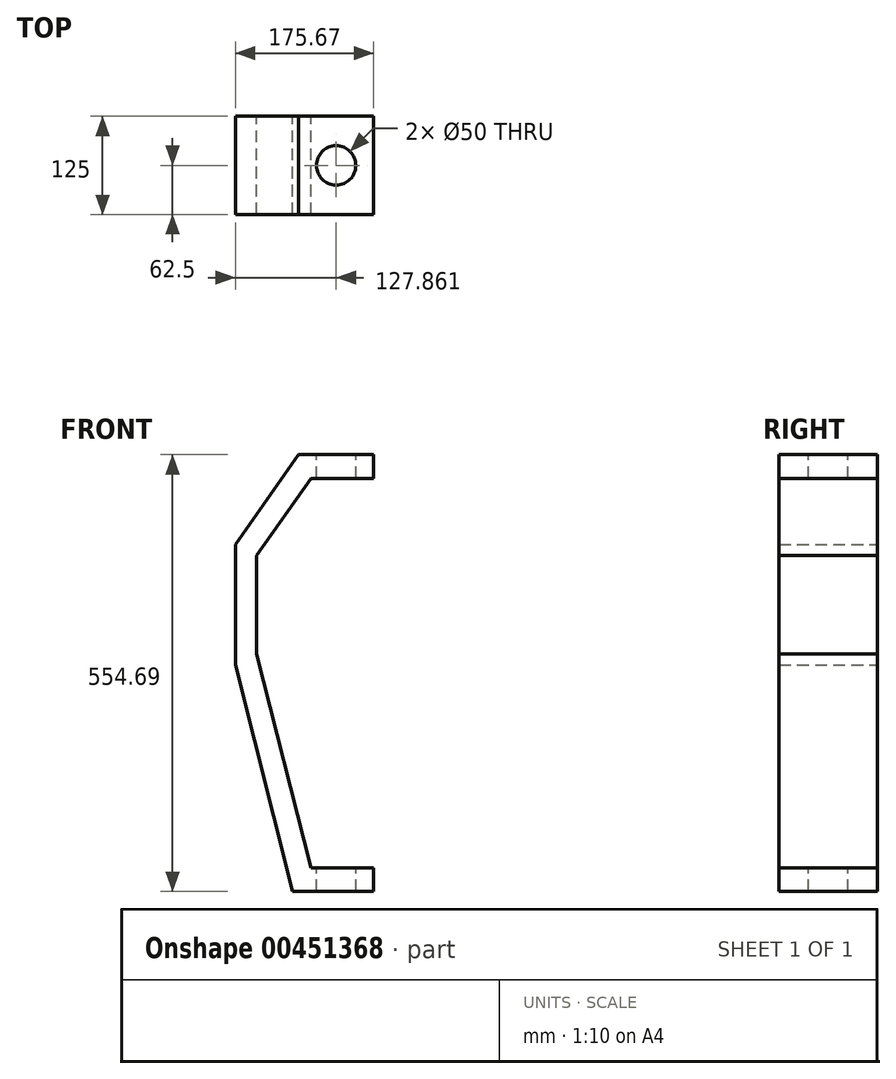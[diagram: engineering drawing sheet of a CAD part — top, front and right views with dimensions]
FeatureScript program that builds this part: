
annotation { "Feature Type Name" : "Feature", "Feature Type Description" : "" }
export const myFeature = defineFeature(function(context is Context, id is Id, definition is map)
    precondition{}
    {
        {
            var Q0;
            Q0=qCreatedBy(makeId("Front.planeOp"),FACE);
            var sketch = newSketch(context, id + "F0", { "sketchPlane" : qUnion([Q0])});
            skLineSegment(sketch, "E0", {"start": v(0, -62.5) * mm, "end": v(0, 62.5) * mm});
            skLineSegment(sketch, "E1", {"start": v(0, 62.5) * mm, "end": v(68.83, 160.8) * mm});
            skLineSegment(sketch, "E2", {"start": v(68.83, 160.8) * mm, "end": v(148.83, 160.8) * mm});
            skLineSegment(sketch, "E3", {"start": v(148.83, 160.8) * mm, "end": v(148.83, 190.8) * mm});
            skLineSegment(sketch, "E4", {"start": v(68.83, 160.8) * mm, "end": v(53.21, 190.8) * mm, "construction": true});
            skLineSegment(sketch, "E5", {"start": v(148.83, 190.8) * mm, "end": v(53.21, 190.8) * mm});
            skLineSegment(sketch, "E6", {"start": v(0, 62.5) * mm, "end": v(-26.84, 76.47) * mm, "construction": true});
            skLineSegment(sketch, "E7", {"start": v(53.21, 190.8) * mm, "end": v(-26.84, 76.47) * mm});
            skLineSegment(sketch, "E8.MirrorCS", {"start": v(0, -62.5) * mm, "end": v(-26.84, -76.47) * mm, "construction": true});
            skLineSegment(sketch, "E9", {"start": v(-26.84, 76.47) * mm, "end": v(-26.84, -76.47) * mm});
            skLineSegment(sketch, "E10", {"start": v(108.83, 160.8) * mm, "end": v(108.83, -333.89) * mm, "construction": true});
            skLineSegment(sketch, "E11", {"start": v(68.83, -333.89) * mm, "end": v(148.83, -333.89) * mm});
            skLineSegment(sketch, "E12", {"start": v(0, -62.5) * mm, "end": v(68.83, -333.89) * mm});
            skLineSegment(sketch, "E13", {"start": v(148.83, -333.89) * mm, "end": v(148.83, -363.89) * mm});
            skLineSegment(sketch, "E14", {"start": v(148.83, -363.89) * mm, "end": v(45.8, -363.89) * mm});
            skLineSegment(sketch, "E15", {"start": v(68.83, -333.89) * mm, "end": v(45.8, -363.89) * mm, "construction": true});
            skLineSegment(sketch, "E16", {"start": v(45.8, -363.89) * mm, "end": v(-26.84, -76.47) * mm});
            skSolve(sketch);
        }
        {
            var Q0;
            Q0=makeQuery(id+"F0.imprint","IMPRINT",FACE,{"disambiguationData":[TD([[makeQuery(id+"F0.imprint","IMPRINT",EDGE,{"derivedFrom":sQuery(id+"F0.wireOp",EDGE,"E0")}),1.0]])]});
            extrude(context, id + "F1", {"entities" : qUnion([Q0]), "depth" : 125 * mm, "symmetric" : true});
        }
        {
            var Q0;
            Q0=makeQuery(id+"F1.opExtrude","SWEPT_FACE",FACE,{"disambiguationData":[OSD([sQuery(id+"F0.wireOp",EDGE,"E5")])]});
            var sketch = newSketch(context, id + "F2", { "sketchPlane" : qUnion([Q0])});
            skCircle(sketch, "E17", {"center": v(101.02, 0) * mm, "radius": 25 * mm});
            skPoint(sketch, "E17.centerSnap0", {"position": v(53.21, 0) * mm});
            skPoint(sketch, "E17.centerSnap1", {"position": v(101.02, 62.5) * mm});
            skSolve(sketch);
        }
        {
            var Q0;
            Q0=sQuery(id+"F2.wireOp",VERTEX,"E17.center");
            var Q1;
            Q1=makeQuery(id+"F1.opExtrude","SWEPT_BODY",BODY,{"disambiguationData":[OSD([sQuery(id+"F0.wireOp",EDGE,"E0"),sQuery(id+"F0.wireOp",EDGE,"E1"),sQuery(id+"F0.wireOp",EDGE,"E2"),sQuery(id+"F0.wireOp",EDGE,"E3"),sQuery(id+"F0.wireOp",EDGE,"E5"),sQuery(id+"F0.wireOp",EDGE,"E7"),sQuery(id+"F0.wireOp",EDGE,"E9"),sQuery(id+"F0.wireOp",EDGE,"E11"),sQuery(id+"F0.wireOp",EDGE,"E12"),sQuery(id+"F0.wireOp",EDGE,"E13"),sQuery(id+"F0.wireOp",EDGE,"E14"),sQuery(id+"F0.wireOp",EDGE,"E16")])]});
            hole(context, id + "F3", {"style" : HoleStyle.SIMPLE, "endStyle" : HoleEndStyle.THROUGH, "holeDiameter" : 50 * mm, "isTappedThrough" : true, "tappedDepth" : 12 * mm, "tapClearance" : 3, "locations" : qUnion([Q0]), "scope" : qUnion([Q1])});
        }
    });
